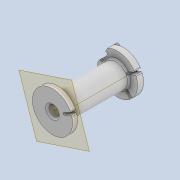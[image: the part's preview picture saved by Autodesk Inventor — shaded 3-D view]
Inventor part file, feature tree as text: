
AUTODESK INVENTOR PART (.ipt)
format: ipt  version: 2020 (Build 240168000, 168)  size: 513,024 bytes
history: native  units: mm
features: sketch x17, extrude x15, projected_geometry x13, fillet x9, other x4, thicken_offset x3, plane x2, chamfer x2, sweep x1, reference x1
ambient origin geometry x8: Origin, YZ Plane, XZ Plane, XY Plane, X Axis, Y Axis, Z Axis, Center Point
bodies: Solid1 (feature_tree)
feature tree (67):
  extrude  "Extrusion1"  Depth=12.0mm
  extrude  "Extrusion2"  Depth=1.0mm
  extrude  "Extrusion3"  Depth=18.0mm TaperAngle=0.0deg
  sketch  "3D Sketch1"
  plane  "Work Plane1"
  sweep  "Sweep1"
  extrude  "Extrusion4"  Depth=0.5mm
  extrude  "Extrusion5"  TaperAngle=0.0deg  [1 undecoded]
  extrude  "Extrusion6"  Depth=0.7mm
  thicken_offset  "Thicken1"
  thicken_offset  "Thicken2"
  extrude  "Extrusion7"  Depth=1.0mm
  extrude  "Extrusion8"  Depth=1.0mm TaperAngle=0.0deg
  extrude  "Extrusion9"  Depth=8.0mm
  chamfer  "Chamfer1"  Distance=2.0mm
  fillet  "Fillet7"  Radius=0.8mm
  fillet  "Fillet8"  Radius=0.8mm
  extrude  "Extrusion10"  Depth=0.5mm
  extrude  "Extrusion11"  Depth=4.0mm
  extrude  "Extrusion13"  Depth=4.0mm
  fillet  "Fillet10"  Radius=0.8mm
  fillet  "Fillet11"  Radius=0.5mm
  fillet  "Fillet12"  Radius=0.5mm
  fillet  "Fillet13"  Radius=3.490659mm
  fillet  "Fillet14"  Radius=2.2mm
  thicken_offset  "Thicken3"
  chamfer  "Chamfer2"  Distance=2.0mm
  plane  "Work Plane2"
  extrude  "Extrusion14"  Depth=0.5mm
  extrude  "Extrusion15"  Depth=0.5mm
  extrude  "Extrusion16"  Depth=0.5mm TaperAngle=0.0deg
  fillet  "Fillet15"  Radius=0.8mm
  fillet  "Fillet16"  Radius=3.0mm
  sketch  "Sketch1"  dims[d0=3.0mm d1=12.0mm]
  reference  "Reference1"
  sketch  "Sketch2"  dims[d2=1.0mm d3=0.0mm d4=3.0mm]
  sketch  "Sketch3"  dims[d5=7.0mm d6=18.0mm d7=0.0mm]
  projected_geometry  "Projected Loop1"
  other  "Helical Curve2"
  sketch  "Sketch4"  dims[d8=1.0mm d9=0.0mm d14=18.0mm d15=160.0mm d16=7.0mm d17=0.0mm]
  projected_geometry  "Projected Loop2"
  projected_geometry  "Projected Loop3"
  sketch  "Sketch5"  dims[d18=0.5mm d19=0.7mm]
  projected_geometry  "Projected Loop4"
  sketch  "Sketch6"  dims[d20=0.5mm d21=0.0mm d22=0.0mm]
  projected_geometry  "Projected Loop5"
  sketch  "Sketch7"  dims[d23=5.0mm d24=0.7mm]
  projected_geometry  "Projected Loop6"
  sketch  "Sketch8"  dims[d25=1.0mm d26=0.0mm d27=5.0mm]
  projected_geometry  "Projected Loop7"
  sketch  "Sketch9"  dims[d28=0.7mm d29=1.0mm d30=0.0mm]
  projected_geometry  "Projected Loop8"
  sketch  "Sketch10"  dims[d37=30.0deg d38=8.0mm]
  projected_geometry  "Projected Loop9"
  sketch  "Sketch11"  dims[d39=6.0mm d40=2.0mm d41=0.0mm d42=0.8mm d43=0.8mm]
  projected_geometry  "Projected Loop10"
  sketch  "Sketch12"  dims[d44=0.5mm d45=0.5mm]
  projected_geometry  "Projected Loop11"
  sketch  "Sketch14"  dims[d46=4.0mm d47=0.0mm d48=1.4mm]
  projected_geometry  "Projected Loop13"
  sketch  "Sketch15"  dims[d49=4.0mm d50=0.0mm d51=4.0mm d52=0.8mm d53=0.0mm]
  projected_geometry  "Projected Loop14"
  sketch  "Sketch16"  dims[d54=0.5mm d55=2.0mm d56=45.0deg d57=0.5mm d58=0.5mm d59=3.490659mm d60=2.2mm]
  sketch  "Sketch17"  dims[d61=0.7mm d62=2.0mm d63=0.0mm d64=5.0mm d65=1.6mm d66=2.0mm d67=0.0mm d72=0.8mm d73=3.0mm d74=5.0mm d75=2.0mm d76=0.0mm d77=1.0mm d78=0.3mm d79=0.1mm d80=0.3mm d81=0.4mm d82=0.05mm d83=0.05mm d84=0.5mm d85=2.0mm d86=45.0deg d87=-0.5mm d88=7.0mm d89=20.0mm d90=0.0mm d91=10.0mm d92=0.0mm d93=4.0mm d94=0.0mm d95=0.25mm d96=0.5mm]
  parser-record x1  (decoder bookkeeping rows leaked as tree rows — omitted from the tree; the rows remain in map.json)
  other  "tip2_ass_t1.iam"
  other  "bearing_3_6_2:1"
note: 1 required parameter value undecoded (feature->parameter linkage not recoverable at this tier; creation-order binding heuristic only, values carry confidence <= 0.55)
note: 1 file-system path scrubbed to <path> (originals preserved in map.json)
